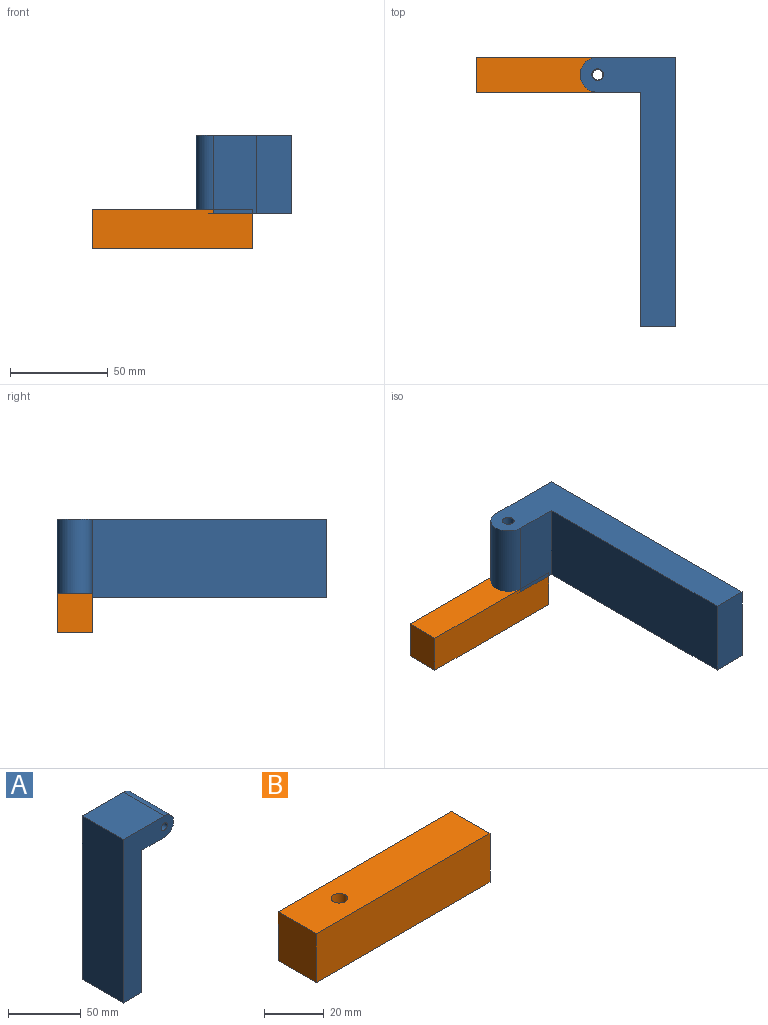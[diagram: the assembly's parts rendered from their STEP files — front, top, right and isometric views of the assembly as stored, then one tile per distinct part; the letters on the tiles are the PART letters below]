
ASSEMBLY  parts=2 mates=1
PART A: 9 faces, bbox 49x40x138 mm
  f0: plane 120x40mm, normal (1,0,0), area 4800mm2, adj f1,f5,f7,f8
  f1: plane 40x22mm, normal (0,0,-1), area 880mm2, adj f0,f2,f7,f8
  f2: cylinder r=9mm len=40mm, axis (0,1,0), area 1131mm2, adj f1,f3,f7,f8
  f3: plane 40x40mm, normal (0,0,1), area 1600mm2, adj f2,f4,f7,f8
  f4: plane 138x40mm, normal (-1,0,0), area 5520mm2, adj f3,f5,f7,f8
  f5: plane 40x18mm, normal (0,0,-1), area 720mm2, adj f0,f4,f7,f8
  f6: cylinder r=3mm len=40mm, axis (0,1,0), area 754mm2, adj f7,f8
  f7: plane 138x49mm, normal (0,-1,0), area 2979mm2, adj f0,f1,f2,f3,f4,f5,f6
  f8: plane 138x49mm, normal (0,1,0), area 2979mm2, adj f0,f1,f2,f3,f4,f5,f6
PART B: 7 faces, bbox 82.2x18x20 mm
  f0: plane 20x18mm, normal (-1,0,0), area 360mm2, adj f1,f3,f4,f5
  f1: plane 82.24x18mm, normal (0,0,-1), area 1456.6mm2, adj f0,f2,f4,f5,f6
  f2: plane 20x18mm, normal (1,0,0), area 360mm2, adj f1,f3,f4,f5
  f3: plane 82.24x18mm, normal (0,0,1), area 1456.6mm2, adj f0,f2,f4,f5,f6
  f4: plane 82.24x20mm, normal (0,-1,0), area 1644.7mm2, adj f0,f1,f2,f3
  f5: plane 82.24x20mm, normal (0,1,0), area 1644.7mm2, adj f0,f1,f2,f3
  f6: cylinder r=2.74mm len=20mm, axis (0,0,-1), area 344.5mm2, adj f1,f3
PLACE A rot(axis=(0,-0.71,-0.71),180deg) t=(87.37,-0.43,80.75)mm
PLACE B rot(axis=(0,0,-1),180deg) t=(67.42,-0.44,22.75)mm fixed
MATE cylindrical A.f2 <-> B.f6  axis (0,0,-1) through (47.37,8.56,40.75)mm
